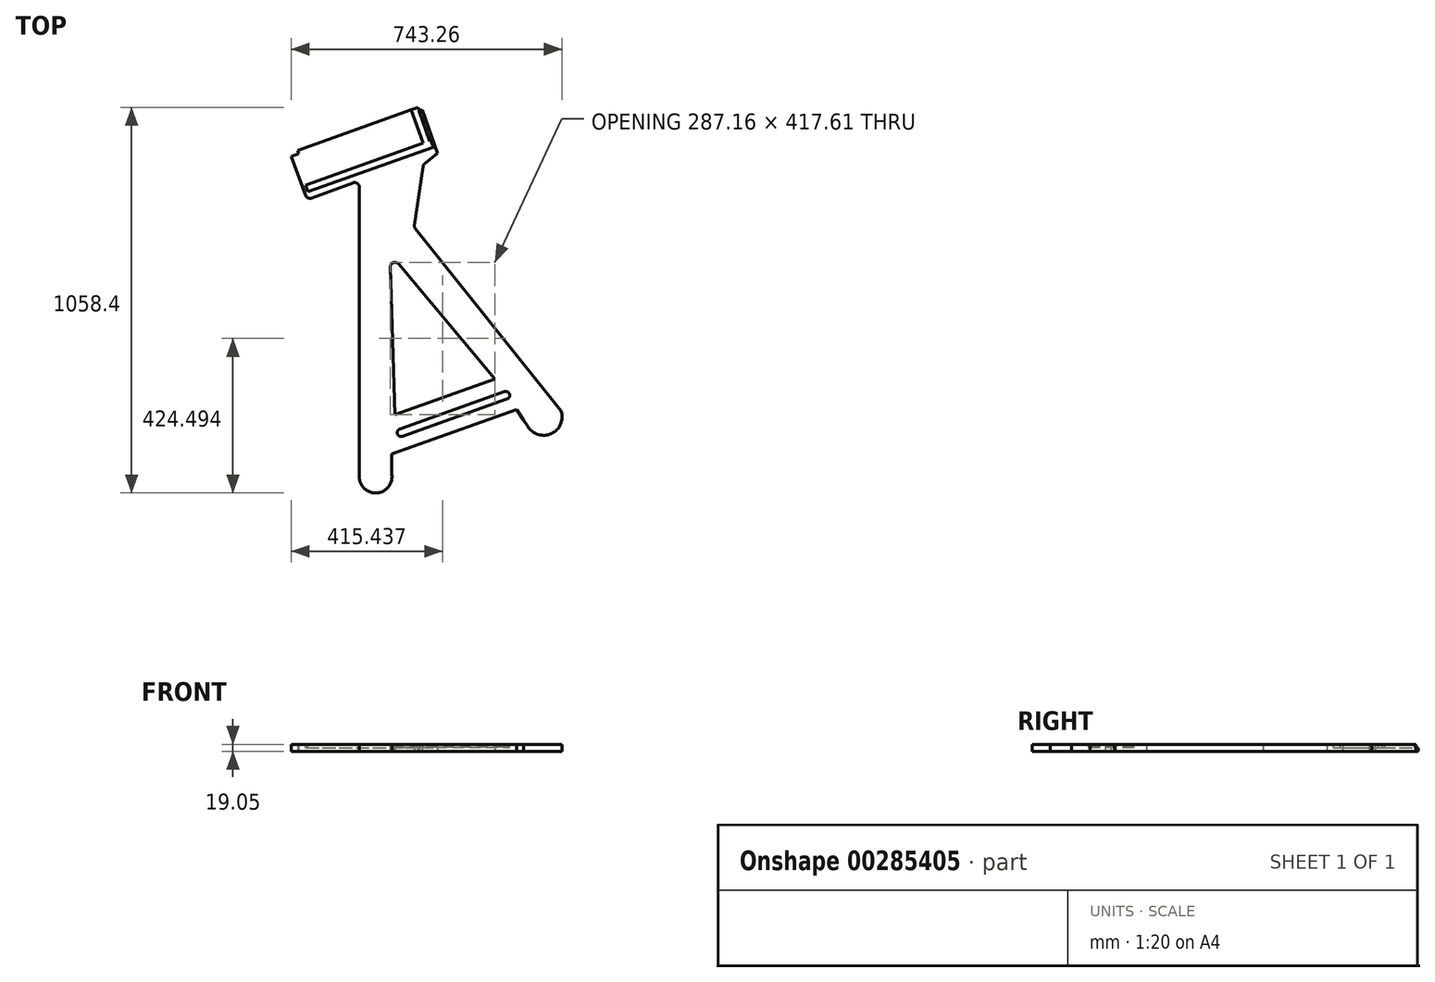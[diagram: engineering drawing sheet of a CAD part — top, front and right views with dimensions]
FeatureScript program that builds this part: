
annotation { "Feature Type Name" : "Feature", "Feature Type Description" : "" }
export const myFeature = defineFeature(function(context is Context, id is Id, definition is map)
    precondition{}
    {
        {
            var Q0;
            Q0=qCreatedBy(makeId("Top.planeOp"),FACE);
            var sketch = newSketch(context, id + "F0", { "sketchPlane" : qUnion([Q0])});
            skLineSegment(sketch, "E0", {"start": v(-306.62, -10.3) * mm, "end": v(-306.88, -10.27) * mm});
            skLineSegment(sketch, "E1", {"start": v(727.27, -283.58) * mm, "end": v(727.27, 427.9) * mm});
            skPoint(sketch, "E2.visualSharp", {"position": v(727.27, -334.1) * mm});
            skPoint(sketch, "E3.visualSharp", {"position": v(828.87, -334.66) * mm});
            skLineSegment(sketch, "E4", {"start": v(902.24, 568.5) * mm, "end": v(878.6, 406.65) * mm});
            skLineSegment(sketch, "E5", {"start": v(727.27, 427.9) * mm, "end": v(727.27, 511.3) * mm});
            skLineSegment(sketch, "E6", {"start": v(710.18, 523.22) * mm, "end": v(596.17, 481.24) * mm});
            skLineSegment(sketch, "E7", {"start": v(579.87, 488.77) * mm, "end": v(540.37, 596.03) * mm});
            skLineSegment(sketch, "E8", {"start": v(540.37, 596.03) * mm, "end": v(561.03, 603.39) * mm});
            skLineSegment(sketch, "E9", {"start": v(899.3, 723.83) * mm, "end": v(941.9, 604.19) * mm});
            skLineSegment(sketch, "E10", {"start": v(906.95, 576.64) * mm, "end": v(941.9, 604.19) * mm});
            skLineSegment(sketch, "E11", {"start": v(540.37, 596.03) * mm, "end": v(561.03, 603.39) * mm, "construction": true});
            skPoint(sketch, "E12.visualSharp", {"position": v(1175.92, -180.14) * mm});
            skLineSegment(sketch, "E13", {"start": v(825.36, -112.6) * mm, "end": v(812.23, 291.9) * mm});
            skLineSegment(sketch, "E14", {"start": v(834.65, 300.48) * mm, "end": v(1099.39, -15.04) * mm});
            skPoint(sketch, "E15.visualSharp", {"position": v(811.04, 328.62) * mm});
            skArc(sketch, "E15.filletArc", {"start": v(834.65, 300.48) * mm, "mid": v(820.38, 304.18) * mm, "end": v(812.23, 291.9) * mm});
            skLineSegment(sketch, "E16", {"start": v(584.25, 476.85) * mm, "end": v(941.9, 604.19) * mm, "construction": true});
            skLineSegment(sketch, "E17", {"start": v(881.25, 396.88) * mm, "end": v(1280.84, -102.55) * mm});
            skLineSegment(sketch, "E18", {"start": v(1185.54, -137.77) * mm, "end": v(1280.84, -102.55) * mm, "construction": true});
            skArc(sketch, "E19", {"start": v(1189.3, -145.4) * mm, "mid": v(1254.36, -165.18) * mm, "end": v(1280.84, -102.55) * mm});
            skLineSegment(sketch, "E20", {"start": v(816.46, -278.75) * mm, "end": v(816.46, -221.1) * mm});
            skLineSegment(sketch, "E21", {"start": v(923.23, 732.35) * mm, "end": v(1268.85, -238.36) * mm, "construction": true});
            skPoint(sketch, "E22.visualSharp", {"position": v(1185.54, -137.77) * mm});
            skPoint(sketch, "E23.visualSharp", {"position": v(877.8, 401.2) * mm});
            skArc(sketch, "E23.filletArc", {"start": v(878.6, 406.65) * mm, "mid": v(878.9, 401.5) * mm, "end": v(881.25, 396.88) * mm});
            skPoint(sketch, "E24.visualSharp", {"position": v(902.97, 573.5) * mm});
            skArc(sketch, "E24.filletArc", {"start": v(906.95, 576.64) * mm, "mid": v(903.81, 573.02) * mm, "end": v(902.24, 568.5) * mm});
            skArc(sketch, "E25.filletArc", {"start": v(727.27, 511.3) * mm, "mid": v(721.83, 521.72) * mm, "end": v(710.18, 523.22) * mm});
            skLineSegment(sketch, "E26", {"start": v(557.84, 612.36) * mm, "end": v(888.53, 730.1) * mm});
            skLineSegment(sketch, "E27", {"start": v(557.84, 612.36) * mm, "end": v(561.03, 603.39) * mm});
            skLineSegment(sketch, "E28", {"start": v(888.53, 730.1) * mm, "end": v(891.73, 721.13) * mm});
            skLineSegment(sketch, "E29.trimOffspring", {"start": v(891.73, 721.13) * mm, "end": v(899.3, 723.83) * mm, "construction": true});
            skLineSegment(sketch, "E30.trimOffspring", {"start": v(891.73, 721.13) * mm, "end": v(899.3, 723.83) * mm});
            skLineSegment(sketch, "E31", {"start": v(1189.3, -145.4) * mm, "end": v(1178.65, -128.04) * mm});
            skLineSegment(sketch, "E32", {"start": v(540.37, 596.03) * mm, "end": v(914.16, -419.2) * mm, "construction": true});
            skLineSegment(sketch, "E33", {"start": v(816.46, -221.1) * mm, "end": v(1159.46, -98.97) * mm});
            skLineSegment(sketch, "E34", {"start": v(1178.65, -128.04) * mm, "end": v(1159.46, -98.97) * mm});
            skLineSegment(sketch, "E35", {"start": v(825.36, -112.6) * mm, "end": v(1099.39, -15.04) * mm});
            skArc(sketch, "E36", {"start": v(727.27, -283.58) * mm, "mid": v(774.4, -328.24) * mm, "end": v(816.46, -278.75) * mm});
            skLineSegment(sketch, "E37", {"start": v(1247.81, -179.28) * mm, "end": v(691.82, -377.24) * mm, "construction": true});
            skPoint(sketch, "E38.visualSharp", {"position": v(584.25, 476.85) * mm});
            skArc(sketch, "E38.filletArc", {"start": v(579.87, 488.77) * mm, "mid": v(586.46, 481.63) * mm, "end": v(596.17, 481.24) * mm});
            skSolve(sketch);
        }
        {
            var Q0;
            Q0=makeQuery(id+"F0.imprint","IMPRINT",FACE,{"disambiguationData":[TD([[makeQuery(id+"F0.imprint","IMPRINT",EDGE,{"derivedFrom":sQuery(id+"F0.wireOp",EDGE,"oAVC5DI8-kh1G-Qbfy-uwvq-Txyh6lFHP0Ui")}),1.0]])]});
            var Q1;
            Q1=makeQuery(id+"F0.imprint","IMPRINT",FACE,{"disambiguationData":[TD([[makeQuery(id+"F0.imprint","IMPRINT",EDGE,{"derivedFrom":sQuery(id+"F0.wireOp",EDGE,"E1")}),-1.0]])]});
            extrude(context, id + "F1", {"entities" : qUnion([Q0, Q1]), "depth" : 19.05 * mm});
        }
        {
            var Q0;
            Q0=makeQuery(id+"F1.opExtrude","CAP_FACE",FACE,{"disambiguationData":[OSD([sQuery(id+"F0.wireOp",EDGE,"E1"),sQuery(id+"F0.wireOp",EDGE,"G0y4bu0m-BWtu-Z1BD-zRkf-oovVnx2JfWYb"),sQuery(id+"F0.wireOp",EDGE,"JKyS3Y8j-kBsw-wtws-iH0O-fFm78A80juFg"),sQuery(id+"F0.wireOp",EDGE,"7wI2reVj-oknS-nbr6-NEhj-tmmQak3yPgpr"),sQuery(id+"F0.wireOp",EDGE,"OE1zSFFg-K3dP-ErGM-cdOK-dd3cl9o4Xoav"),sQuery(id+"F0.wireOp",EDGE,"GfWBLkyY-Kkl3-p4zT-R0sz-4QZl2egGdYTh"),sQuery(id+"F0.wireOp",EDGE,"E2.filletArc"),sQuery(id+"F0.wireOp",EDGE,"E3.filletArc"),sQuery(id+"F0.wireOp",EDGE,"e34a206c-400c-4626-8d55-ad7425813022.filletArc"),sQuery(id+"F0.wireOp",EDGE,"E4"),sQuery(id+"F0.wireOp",EDGE,"E5"),sQuery(id+"F0.wireOp",EDGE,"E6"),sQuery(id+"F0.wireOp",EDGE,"E7"),sQuery(id+"F0.wireOp",EDGE,"E8"),sQuery(id+"F0.wireOp",EDGE,"E9"),sQuery(id+"F0.wireOp",EDGE,"E10"),sQuery(id+"F0.wireOp",EDGE,"2dwz68pA-47ym-ayAl-zs7R-NUUpSdQx5Jh0"),sQuery(id+"F0.wireOp",EDGE,"E12.filletArc")])],"isStart":false});
            var sketch = newSketch(context, id + "F2", { "sketchPlane" : qUnion([Q0])});
            skLineSegment(sketch, "E39", {"start": v(845.7, -172.6) * mm, "end": v(1132.84, -70.36) * mm});
            skLineSegment(sketch, "E40", {"start": v(1125.6, -50.02) * mm, "end": v(838.45, -152.25) * mm});
            skLineSegment(sketch, "E41.0", {"start": v(540.37, 596.03) * mm, "end": v(777.78, -334.38) * mm, "construction": true});
            skLineSegment(sketch, "E42.0", {"start": v(878.4, -322.07) * mm, "end": v(1232.82, -195.88) * mm, "construction": true});
            skArc(sketch, "E43", {"start": v(838.45, -152.25) * mm, "mid": v(831.9, -166.04) * mm, "end": v(845.7, -172.6) * mm});
            skArc(sketch, "E44", {"start": v(1132.84, -70.36) * mm, "mid": v(1139.38, -56.56) * mm, "end": v(1125.6, -50.02) * mm});
            skSolve(sketch);
        }
        {
            var Q0;
            Q0 = qSketchRegion(id + "F2", true);
            extrude(context, id + "F3", {"entities" : qUnion([Q0]), "operationType" : NewBodyOperationType.REMOVE, "oppositeDirection" : true, "depth" : 8.47 * mm});
        }
        {
            var Q0;
            Q0=makeQuery(id+"F1.opExtrude","CAP_FACE",FACE,{"disambiguationData":[OSD([sQuery(id+"F0.wireOp",EDGE,"E1"),sQuery(id+"F0.wireOp",EDGE,"E2.filletArc"),sQuery(id+"F0.wireOp",EDGE,"E3.filletArc"),sQuery(id+"F0.wireOp",EDGE,"E4"),sQuery(id+"F0.wireOp",EDGE,"E5"),sQuery(id+"F0.wireOp",EDGE,"E6"),sQuery(id+"F0.wireOp",EDGE,"E7"),sQuery(id+"F0.wireOp",EDGE,"E8"),sQuery(id+"F0.wireOp",EDGE,"E9"),sQuery(id+"F0.wireOp",EDGE,"E10"),sQuery(id+"F0.wireOp",EDGE,"E13"),sQuery(id+"F0.wireOp",EDGE,"E14"),sQuery(id+"F0.wireOp",EDGE,"E15.filletArc"),sQuery(id+"F0.wireOp",EDGE,"O38EEshE-uP5z-nFdx-e3qj-11sBSmLcHE88"),sQuery(id+"F0.wireOp",EDGE,"b6148c74-efb1-4f58-bf84-b4f1c3a6a91b"),sQuery(id+"F0.wireOp",EDGE,"E17"),sQuery(id+"F0.wireOp",EDGE,"E19"),sQuery(id+"F0.wireOp",EDGE,"E20"),sQuery(id+"F0.wireOp",EDGE,"mhekoGqz-hg7g-Awbu-1WS0-d6fdl79PSdHc"),sQuery(id+"F0.wireOp",EDGE,"5Wj1d7Zn-DfYv-PjeH-97pm-uPEhj1uLzUow"),sQuery(id+"F0.wireOp",EDGE,"440a19d6-b247-49e8-bacf-2963a67fc6c6.filletArc"),sQuery(id+"F0.wireOp",EDGE,"E22.filletArc"),sQuery(id+"F0.wireOp",EDGE,"E23.filletArc"),sQuery(id+"F0.wireOp",EDGE,"E24.filletArc"),sQuery(id+"F0.wireOp",EDGE,"E25.filletArc")])],"isStart":false});
            var sketch = newSketch(context, id + "F4", { "sketchPlane" : qUnion([Q0])});
            skLineSegment(sketch, "E45.bottom", {"start": v(586.26, 498.62) * mm, "end": v(926.44, 619.74) * mm});
            skLineSegment(sketch, "E45.top", {"start": v(579.7, 517.04) * mm, "end": v(902.22, 631.88) * mm});
            skLineSegment(sketch, "E45.left", {"start": v(586.26, 498.62) * mm, "end": v(579.7, 517.04) * mm});
            skLineSegment(sketch, "E46", {"start": v(920, 637.82) * mm, "end": v(891.85, 716.88) * mm});
            skLineSegment(sketch, "E47", {"start": v(874.2, 710.6) * mm, "end": v(902.22, 631.88) * mm});
            skLineSegment(sketch, "E48", {"start": v(874.2, 710.6) * mm, "end": v(869.65, 723.38) * mm});
            skPoint(sketch, "E49.endSnap0", {"position": v(895.51, 722.48) * mm});
            skLineSegment(sketch, "E50", {"start": v(891.85, 716.88) * mm, "end": v(890.5, 720.7) * mm});
            skLineSegment(sketch, "E51", {"start": v(891.73, 721.13) * mm, "end": v(890.5, 720.7) * mm});
            skLineSegment(sketch, "E52", {"start": v(891.73, 721.13) * mm, "end": v(888.53, 730.1) * mm});
            skLineSegment(sketch, "E53", {"start": v(888.53, 730.1) * mm, "end": v(869.65, 723.38) * mm});
            skLineSegment(sketch, "E54", {"start": v(926.44, 619.74) * mm, "end": v(930.6, 621.22) * mm});
            skLineSegment(sketch, "E55", {"start": v(930.6, 621.22) * mm, "end": v(924.16, 639.3) * mm});
            skLineSegment(sketch, "E56", {"start": v(924.16, 639.3) * mm, "end": v(920, 637.82) * mm});
            skPoint(sketch, "E57.orphan", {"position": v(920.95, 638.16) * mm});
            skPoint(sketch, "E58.orphan", {"position": v(919.88, 638.16) * mm});
            skSolve(sketch);
        }
        {
            var Q0;
            Q0 = qSketchRegion(id + "F4", true);
            extrude(context, id + "F5", {"entities" : qUnion([Q0]), "operationType" : NewBodyOperationType.REMOVE, "oppositeDirection" : true, "depth" : 9.52 * mm});
        }
    });
